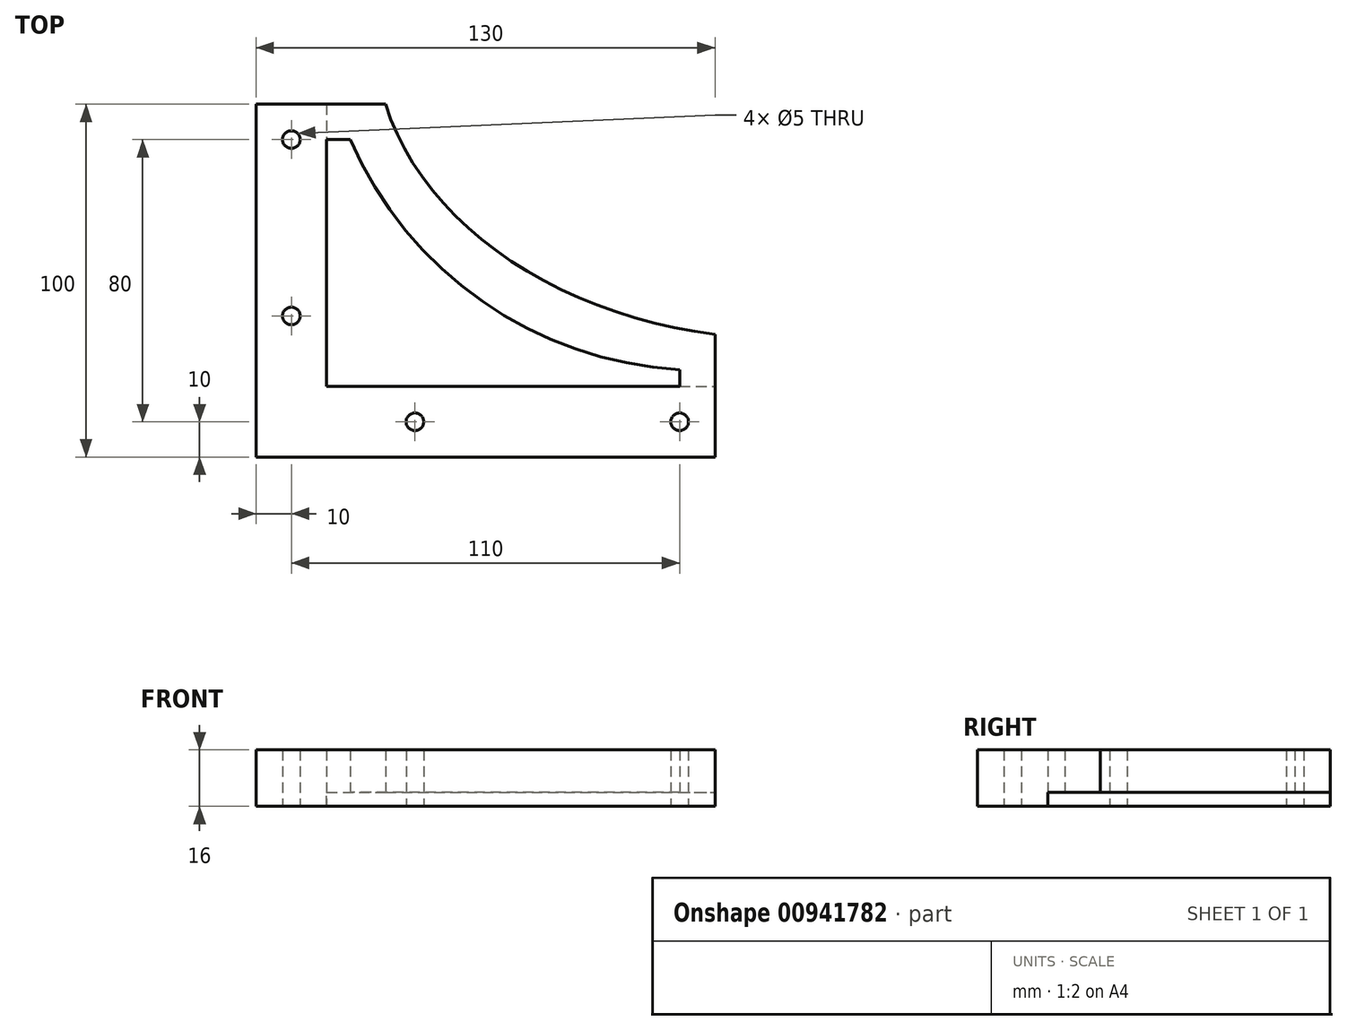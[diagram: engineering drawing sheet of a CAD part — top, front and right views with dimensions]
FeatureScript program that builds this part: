
annotation { "Feature Type Name" : "Feature", "Feature Type Description" : "" }
export const myFeature = defineFeature(function(context is Context, id is Id, definition is map)
    precondition{}
    {
        {
            var Q0;
            Q0=qCreatedBy(makeId("Top.planeOp"),FACE);
            var sketch = newSketch(context, id + "F0", { "sketchPlane" : qUnion([Q0])});
            skEllipticalArc(sketch, "E0", {});
            skLineSegment(sketch, "E1", {"start": v(-116.5, 0) * mm, "end": v(-116.5, -86.5) * mm});
            skPoint(sketch, "E1.endSnap0", {"position": v(0, -86.5) * mm});
            skLineSegment(sketch, "E2", {"start": v(-116.5, -86.5) * mm, "end": v(0, -86.5) * mm});
            skLineSegment(sketch, "E3", {"start": v(-116.5, 0) * mm, "end": v(-130, 0) * mm});
            skLineSegment(sketch, "E4", {"start": v(-130, 0) * mm, "end": v(-130, -100) * mm});
            skLineSegment(sketch, "E5", {"start": v(-130, -100) * mm, "end": v(0, -100) * mm});
            skLineSegment(sketch, "E6", {"start": v(0, -100) * mm, "end": v(0, -86.5) * mm});
            const initialGuessF0  = {"E0": [0, 0, 1, 0, 0.1165, 0.0865, 3.141592653589793, 4.71238898038469]};
            skSetInitialGuess(sketch, initialGuessF0);
            skSolve(sketch);
        }
        {
            var Q0;
            Q0=qSketchRegion(id+"F0",true);
            extrude(context, id + "F1", {"entities" : qUnion([Q0]), "depth" : 12 * mm, "offsetDistance" : 25 * mm});
        }
        {
            var Q0;
            Q0=makeQuery(id+"F1.opExtrude","SWEPT_FACE",FACE,{"disambiguationData":[OSD([sQuery(id+"F0.wireOp",EDGE,"E5")])]});
            var sketch = newSketch(context, id + "F2", { "sketchPlane" : qUnion([Q0])});
            skLineSegment(sketch, "E7.bottom", {"start": v(-130, 16) * mm, "end": v(0, 16) * mm});
            skLineSegment(sketch, "E7.top", {"start": v(-130, -4) * mm, "end": v(0, -4) * mm});
            skLineSegment(sketch, "E7.left", {"start": v(-130, 16) * mm, "end": v(-130, -4) * mm});
            skLineSegment(sketch, "E7.right", {"start": v(0, 16) * mm, "end": v(0, -4) * mm});
            skSolve(sketch);
        }
        {
            var Q0;
            Q0=qSketchRegion(id+"F2",true);
            extrude(context, id + "F3", {"entities" : qUnion([Q0]), "operationType" : NewBodyOperationType.ADD, "depth" : 5 * mm, "offsetDistance" : 25 * mm});
        }
        {
            var Q0;
            Q0=makeQuery(id+"F3.boolean.opBoolean","MERGE",FACE,{"derivedFrom":[makeQuery(id+"F1.opExtrude","SWEPT_FACE",FACE,{"disambiguationData":[OSD([sQuery(id+"F0.wireOp",EDGE,"E4")])]}),makeQuery(id+"F3.opExtrude","SWEPT_FACE",FACE,{"disambiguationData":[OSD([sQuery(id+"F2.wireOp",EDGE,"E7.left")])]})]});
            var sketch = newSketch(context, id + "F4", { "sketchPlane" : qUnion([Q0])});
            skLineSegment(sketch, "E8.bottom", {"start": v(105, 16) * mm, "end": v(0, 16) * mm});
            skLineSegment(sketch, "E8.top", {"start": v(105, -4) * mm, "end": v(0, -4) * mm});
            skLineSegment(sketch, "E8.left", {"start": v(105, 16) * mm, "end": v(105, -4) * mm});
            skLineSegment(sketch, "E8.right", {"start": v(0, 16) * mm, "end": v(0, -4) * mm});
            skSolve(sketch);
        }
        {
            var Q0;
            Q0=qSketchRegion(id+"F4",true);
            extrude(context, id + "F5", {"entities" : qUnion([Q0]), "operationType" : NewBodyOperationType.ADD, "depth" : 5 * mm, "offsetDistance" : 25 * mm});
        }
        {
            var Q0;
            Q0=makeQuery(id+"F5.boolean.opBoolean","MERGE",FACE,{"derivedFrom":[makeQuery(id+"F3.opExtrude","SWEPT_FACE",FACE,{"disambiguationData":[OSD([sQuery(id+"F2.wireOp",EDGE,"E7.bottom")])]}),makeQuery(id+"F5.opExtrude","SWEPT_FACE",FACE,{"disambiguationData":[OSD([sQuery(id+"F4.wireOp",EDGE,"E8.bottom")])]})]});
            var sketch = newSketch(context, id + "F6", { "sketchPlane" : qUnion([Q0])});
            skLineSegment(sketch, "E9", {"start": v(-135, 0) * mm, "end": v(-120, 0) * mm});
            skLineSegment(sketch, "E10", {"start": v(-120, 0) * mm, "end": v(-120, -90) * mm});
            skLineSegment(sketch, "E11", {"start": v(-120, -90) * mm, "end": v(0, -90) * mm});
            skLineSegment(sketch, "E12", {"start": v(0, -90) * mm, "end": v(0, -105) * mm});
            skLineSegment(sketch, "E13", {"start": v(0, -105) * mm, "end": v(-135, -105) * mm});
            skLineSegment(sketch, "E14", {"start": v(-135, -105) * mm, "end": v(-135, 0) * mm});
            skSolve(sketch);
        }
        {
            var Q0;
            Q0=makeQuery(id+"F5.boolean.opBoolean","MERGE",FACE,{"derivedFrom":[makeQuery(id+"F3.opExtrude","SWEPT_FACE",FACE,{"disambiguationData":[OSD([sQuery(id+"F2.wireOp",EDGE,"E7.top")])]}),makeQuery(id+"F5.opExtrude","SWEPT_FACE",FACE,{"disambiguationData":[OSD([sQuery(id+"F4.wireOp",EDGE,"E8.top")])]})]});
            var sketch = newSketch(context, id + "F7", { "sketchPlane" : qUnion([Q0])});
            skLineSegment(sketch, "E15.bottom", {"start": v(-130, 0) * mm, "end": v(-150, 0) * mm});
            skLineSegment(sketch, "E15.top", {"start": v(-130, 120) * mm, "end": v(-150, 120) * mm});
            skLineSegment(sketch, "E15.left", {"start": v(-130, 0) * mm, "end": v(-130, 120) * mm});
            skLineSegment(sketch, "E15.right", {"start": v(-150, 0) * mm, "end": v(-150, 120) * mm});
            skLineSegment(sketch, "E16.bottom", {"start": v(0, 100) * mm, "end": v(-150, 100) * mm});
            skLineSegment(sketch, "E16.top", {"start": v(0, 120) * mm, "end": v(-150, 120) * mm});
            skLineSegment(sketch, "E16.left", {"start": v(0, 100) * mm, "end": v(0, 120) * mm});
            skLineSegment(sketch, "E16.right", {"start": v(-150, 100) * mm, "end": v(-150, 120) * mm});
            skCircle(sketch, "E17", {"center": v(-140, 30) * mm, "radius": 2.5 * mm});
            skCircle(sketch, "E18", {"center": v(-140, 80) * mm, "radius": 2.5 * mm});
            skCircle(sketch, "E19", {"center": v(-105, 110) * mm, "radius": 2.5 * mm});
            skCircle(sketch, "E20", {"center": v(-30, 110) * mm, "radius": 2.5 * mm});
            skSolve(sketch);
        }
        {
            var Q0;
            Q0=qSketchRegion(id+"F7",true);
            extrude(context, id + "F8", {"entities" : qUnion([Q0]), "operationType" : NewBodyOperationType.ADD, "oppositeDirection" : true, "depth" : 25 * mm, "offsetDistance" : 25 * mm});
        }
        {
            var Q0;
            Q0=qSketchRegion(id+"F6",true);
            extrude(context, id + "F9", {"entities" : qUnion([Q0]), "operationType" : NewBodyOperationType.ADD, "depth" : 5 * mm, "offsetDistance" : 25 * mm});
        }
        {
            var Q0;
            Q0=qCreatedBy(makeId("Top.planeOp"),FACE);
            var sketch = newSketch(context, id + "F10", { "sketchPlane" : qUnion([Q0])});
            skLineSegment(sketch, "E21.bottom", {"start": v(-150, 0) * mm, "end": v(0, 0) * mm});
            skLineSegment(sketch, "E21.top", {"start": v(-150, -20) * mm, "end": v(0, -20) * mm});
            skLineSegment(sketch, "E21.left", {"start": v(-150, 0) * mm, "end": v(-150, -20) * mm});
            skLineSegment(sketch, "E21.right", {"start": v(0, 0) * mm, "end": v(0, -20) * mm});
            skLineSegment(sketch, "E22.bottom", {"start": v(0, -120) * mm, "end": v(-20, -120) * mm});
            skLineSegment(sketch, "E22.top", {"start": v(0, 0) * mm, "end": v(-20, 0) * mm});
            skLineSegment(sketch, "E22.left", {"start": v(0, -120) * mm, "end": v(0, 0) * mm});
            skLineSegment(sketch, "E22.right", {"start": v(-20, -120) * mm, "end": v(-20, 0) * mm});
            skSolve(sketch);
        }
        {
            var Q0;
            Q0=qSketchRegion(id+"F10",true);
            extrude(context, id + "F11", {"entities" : qUnion([Q0]), "operationType" : NewBodyOperationType.REMOVE, "endBound" : BoundingType.SYMMETRIC, "oppositeDirection" : true, "depth" : 50 * mm, "offsetDistance" : 25 * mm});
        }
        {
            var Q0;
            Q0=makeQuery(id+"F11.boolean.opBoolean","COPY",FACE,{"derivedFrom":makeQuery(id+"F11.opExtrude","SWEPT_FACE",FACE,{"disambiguationData":[OSD([sQuery(id+"F10.wireOp",EDGE,"E22.right")])]})});
            var sketch = newSketch(context, id + "F12", { "sketchPlane" : qUnion([Q0])});
            skLineSegment(sketch, "E23.bottom", {"start": v(-120, 21) * mm, "end": v(-20, 21) * mm});
            skLineSegment(sketch, "E23.top", {"start": v(-120, 12) * mm, "end": v(-20, 12) * mm});
            skLineSegment(sketch, "E23.left", {"start": v(-120, 21) * mm, "end": v(-120, 12) * mm});
            skLineSegment(sketch, "E23.right", {"start": v(-20, 21) * mm, "end": v(-20, 12) * mm});
            skSolve(sketch);
        }
        {
            var Q0;
            Q0 = qSketchRegion(id + "F12", true);
            extrude(context, id + "F13", {"entities" : qUnion([Q0]), "operationType" : NewBodyOperationType.REMOVE, "oppositeDirection" : true, "depth" : 150 * mm, "offsetDistance" : 25 * mm});
        }
        {
            var Q0;
            Q0=makeQuery(id+"F1.opExtrude","CAP_FACE",FACE,{"disambiguationData":[OSD([sQuery(id+"F0.wireOp",EDGE,"E0"),sQuery(id+"F0.wireOp",EDGE,"E3"),sQuery(id+"F0.wireOp",EDGE,"E4"),sQuery(id+"F0.wireOp",EDGE,"E5"),sQuery(id+"F0.wireOp",EDGE,"E6")])],"isStart":true});
            var sketch = newSketch(context, id + "F14", { "sketchPlane" : qUnion([Q0])});
            skLineSegment(sketch, "E24", {"start": v(-130, 100) * mm, "end": v(-130, 30) * mm});
            skLineSegment(sketch, "E25", {"start": v(-130, 30) * mm, "end": v(-123.34, 30) * mm});
            skLineSegment(sketch, "E26", {"start": v(-30, 95.22) * mm, "end": v(-30, 100) * mm});
            skLineSegment(sketch, "E27", {"start": v(-30, 100) * mm, "end": v(-130, 100) * mm});
            skArc(sketch, "E28", {"start": v(-30, 95.22) * mm, "mid": v(-85.9, 75.82) * mm, "end": v(-123.34, 30) * mm});
            skSolve(sketch);
        }
        {
            var Q0;
            Q0 = qSketchRegion(id + "F14", true);
            extrude(context, id + "F15", {"entities" : qUnion([Q0]), "operationType" : NewBodyOperationType.REMOVE, "oppositeDirection" : true, "depth" : 25 * mm, "offsetDistance" : 25 * mm});
        }
    });
